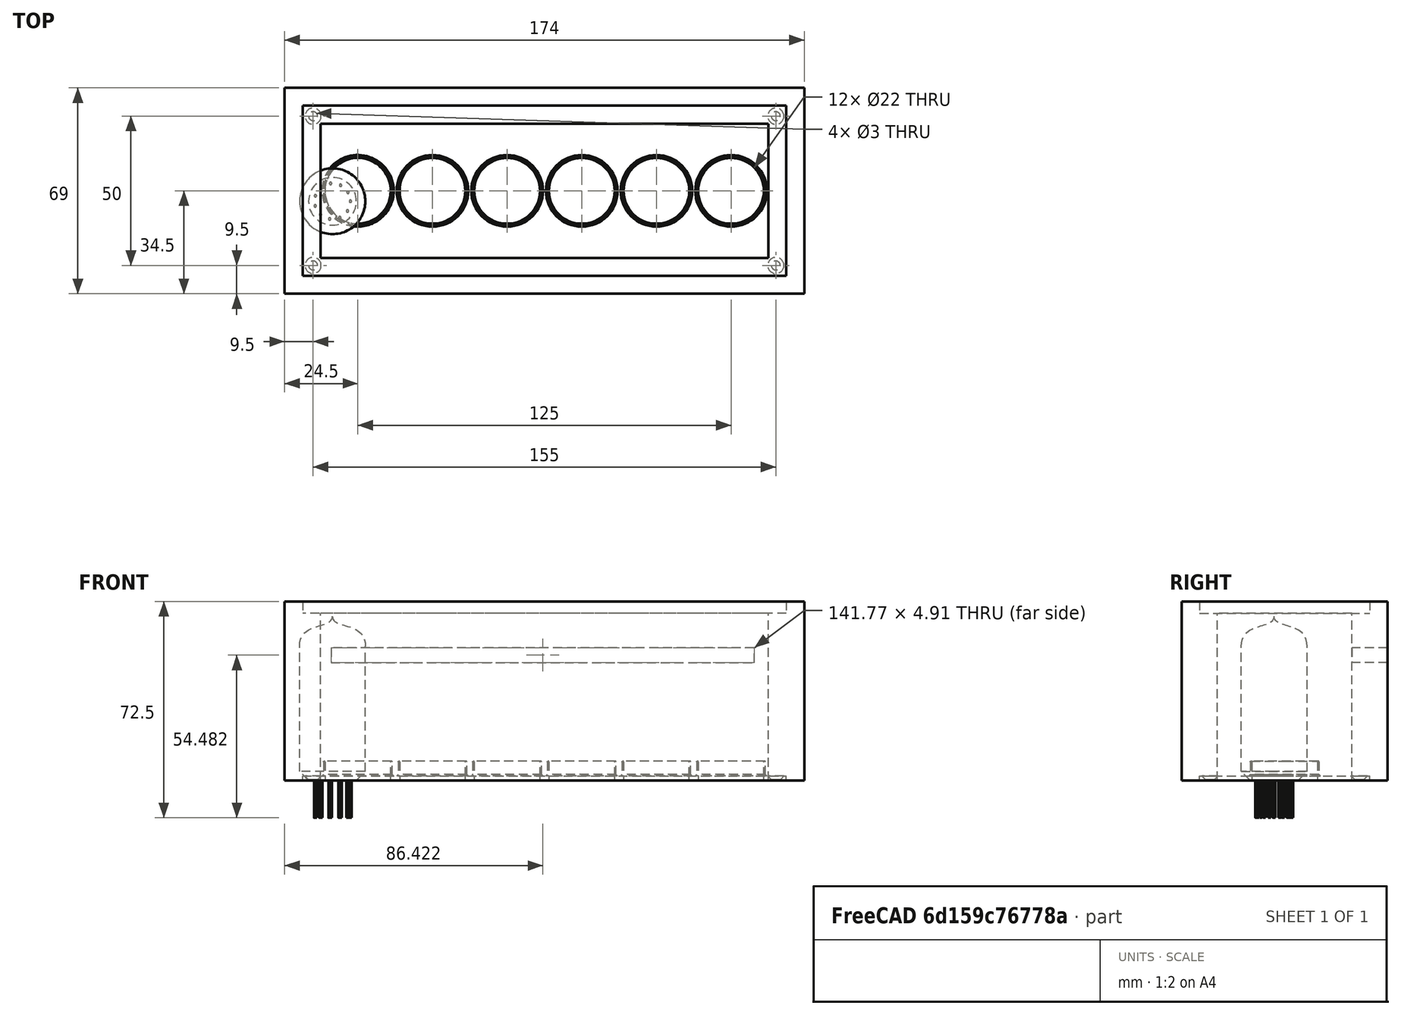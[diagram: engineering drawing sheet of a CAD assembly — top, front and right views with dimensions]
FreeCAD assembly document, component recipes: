
FREECAD ASSEMBLY — COMPONENT RECIPES ("aiometer")

This assembly document has 3 components, labeled P0..P2 below (a component is one placed body or linked part). 3 of them carry a construction recipe — the FreeCAD feature program that regenerates the part from scratch, quoted from this document or its linked companion documents; the rest are supplied as boundary geometry only. No exploded tour is included for this assembly.
COMPONENT P0 — recipe-attached ("Body", modeled in this document).
Construction recipe (the document's own serialized feature program — sketch geometry with constraints, then the solid features built on it; lengths are millimeters unless a unit is written):

FEATURE [Sketcher::SketchObject] Sketch  label="front"
  FullyConstrained = true
  MapMode = 5
  Support = -> [XY_Plane]
  sketch-geometry (4):
    g0: LineSegment StartX=162 StartY=-12 StartZ=0 EndX=150 EndY=0 EndZ=0
    g1: LineSegment StartX=150 StartY=0 StartZ=0 EndX=0 EndY=0 EndZ=0
    g2: LineSegment StartX=0 StartY=0 StartZ=0 EndX=-12 EndY=-12 EndZ=0
    g3: LineSegment StartX=-12 StartY=-12 StartZ=0 EndX=162 EndY=-12 EndZ=0
  constraints (11):
    c: Coincident(g0,g1)
    c: Horizontal(g1)
    c: DistanceX(g1,g1) = 150
    c: DistanceY(g0,g0) = 12
    c: Coincident(g-1,g1)
    c: Coincident(g1,g2)
    c: Coincident(g2,g3)
    c: Coincident(g3,g0)
    c: Horizontal(g3)
    c: Angle(g3,g2) = 0.785398
    c: Angle(g0,g3) = 0.785398
FEATURE [PartDesign::Pad] Pad  label="Front"
  Direction = (0,0,1)
  Length = 60
  Length2 = 10
  Profile = -> Sketch
  ReferenceAxis = -> Sketch [N_Axis]
  Type = 0
FEATURE [Sketcher::SketchObject] Sketch001  label="right"
  ExternalGeometry = -> [Pad,Sketch]
  FullyConstrained = true
  MapMode = 5
  Support = -> [XY_Plane]
  sketch-geometry (4):
    g0: LineSegment StartX=0 StartY=45 StartZ=0 EndX=0 EndY=0 EndZ=0
    g1: LineSegment StartX=0 StartY=0 StartZ=0 EndX=-12 EndY=-12 EndZ=0
    g2: LineSegment StartX=-12 StartY=-12 StartZ=0 EndX=-12 EndY=57 EndZ=0
    g3: LineSegment StartX=-12 StartY=57 StartZ=0 EndX=0 EndY=45 EndZ=0
  constraints (10):
    c: Vertical(g0)
    c: Coincident(g0,g-4)
    c: DistanceY(g0,g0) = 45
    c: Coincident(g0,g1)
    c: Coincident(g1,g2)
    c: Vertical(g2)
    c: Coincident(g2,g3)
    c: Coincident(g3,g0)
    c: Coincident(g1,g-5)
    c: Angle(g2,g3) = 0.785398
FEATURE [PartDesign::Pad] Pad001  label="Right"
  BaseFeature = -> Pad
  Direction = (0,0,1)
  Length = 60
  Length2 = 10
  Profile = -> Sketch001
  ReferenceAxis = -> Sketch001 [N_Axis]
  Type = 0
  expr: Length = Pad.Length
FEATURE [Sketcher::SketchObject] Sketch004  label="left"
  ExternalGeometry = -> [Sketch,Sketch001]
  FullyConstrained = true
  MapMode = 5
  Support = -> [XY_Plane]
  sketch-geometry (4):
    g0: LineSegment StartX=150 StartY=0 StartZ=0 EndX=162 EndY=-12 EndZ=0
    g1: LineSegment StartX=162 StartY=-12 StartZ=0 EndX=162 EndY=57 EndZ=0
    g2: LineSegment StartX=162 StartY=57 StartZ=0 EndX=150 EndY=45 EndZ=0
    g3: LineSegment StartX=150 StartY=45 StartZ=0 EndX=150 EndY=0 EndZ=0
  constraints (10):
    c: Coincident(g-4,g0)
    c: Coincident(g0,g-4)
    c: Coincident(g0,g1)
    c: Vertical(g1)
    c: Coincident(g1,g2)
    c: Coincident(g2,g3)
    c: Coincident(g3,g0)
    c: Vertical(g3)
    c: Equal(g3,g-5)
    c: Equal(g1,g-6)
FEATURE [PartDesign::Pad] Pad004  label="Left"
  BaseFeature = -> Pad001
  Direction = (0,0,1)
  Length = 60
  Length2 = 10
  Profile = -> Sketch004
  ReferenceAxis = -> Sketch004 [N_Axis]
  Type = 0
  expr: Length = Pad.Length
FEATURE [Sketcher::SketchObject] Sketch007  label="back"
  ExternalGeometry = -> [Pad004]
  FullyConstrained = true
  MapMode = 5
  Support = -> [XY_Plane]
  sketch-geometry (4):
    g0: LineSegment StartX=-12 StartY=57 StartZ=0 EndX=162 EndY=57 EndZ=0
    g1: LineSegment StartX=162 StartY=57 StartZ=0 EndX=150 EndY=45 EndZ=0
    g2: LineSegment StartX=150 StartY=45 StartZ=0 EndX=0 EndY=45 EndZ=0
    g3: LineSegment StartX=0 StartY=45 StartZ=0 EndX=-12 EndY=57 EndZ=0
  constraints (8):
    c: Coincident(g0,g-3)
    c: Coincident(g0,g-6)
    c: Coincident(g0,g1)
    c: Coincident(g1,g-5)
    c: Coincident(g1,g2)
    c: Coincident(g2,g-4)
    c: Coincident(g2,g3)
    c: Coincident(g3,g0)
FEATURE [PartDesign::Pad] Pad006  label="Back"
  BaseFeature = -> Pad004
  Direction = (0,0,1)
  Length = 60
  Length2 = 10
  Profile = -> Sketch007
  ReferenceAxis = -> Sketch007 [N_Axis]
  Type = 0
  expr: Length = Pad.Length
FEATURE [Sketcher::SketchObject] Sketch008  label="top_step"
  ExternalGeometry = -> [Pad006]
  FullyConstrained = true
  MapMode = 5
  Placement = pos=(0,0,60) rot=(0,0,1;0rad)
  Support = -> [Pad006]
  sketch-geometry (4):
    g0: LineSegment StartX=-6 StartY=51 StartZ=0 EndX=156 EndY=51 EndZ=0
    g1: LineSegment StartX=156 StartY=51 StartZ=0 EndX=156 EndY=-6 EndZ=0
    g2: LineSegment StartX=156 StartY=-6 StartZ=0 EndX=-6 EndY=-6 EndZ=0
    g3: LineSegment StartX=-6 StartY=-6 StartZ=0 EndX=-6 EndY=51 EndZ=0
  constraints (12):
    c: PointOnObject(g0,g-3)
    c: PointOnObject(g0,g-6)
    c: Horizontal(g0)
    c: Coincident(g0,g1)
    c: PointOnObject(g1,g-5)
    c: Vertical(g1)
    c: Coincident(g1,g2)
    c: PointOnObject(g2,g-4)
    c: Horizontal(g2)
    c: Coincident(g2,g3)
    c: Coincident(g3,g0)
    c: DistanceX(g2,g-4) = 6
FEATURE [PartDesign::Pocket] Pocket  label="Top_step"
  BaseFeature = -> Pad006
  Direction = (0,0,-1)
  Length = 4
  Length2 = 5
  Profile = -> Sketch008
  ReferenceAxis = -> Sketch008 [N_Axis]
  Type = 0
FEATURE [Sketcher::SketchObject] Sketch011
  FullyConstrained = false
  MapMode = 5
  Placement = pos=(0,57,0) rot=(0,0.707107,0.707107;3.14159rad)
  Support = -> [Pad006]
  sketch-geometry (4):
    g0: LineSegment StartX=-145.309 StartY=44.4355 StartZ=0 EndX=-3.53485 EndY=44.4355 EndZ=0
    g1: LineSegment StartX=-3.53485 StartY=44.4355 StartZ=0 EndX=-3.53485 EndY=39.5279 EndZ=0
    g2: LineSegment StartX=-3.53485 StartY=39.5279 StartZ=0 EndX=-145.309 EndY=39.5279 EndZ=0
    g3: LineSegment StartX=-145.309 StartY=39.5279 StartZ=0 EndX=-145.309 EndY=44.4355 EndZ=0
  constraints (8):
    c: Coincident(g0,g1)
    c: Coincident(g1,g2)
    c: Coincident(g2,g3)
    c: Coincident(g3,g0)
    c: Horizontal(g0)
    c: Horizontal(g2)
    c: Vertical(g1)
    c: Vertical(g3)
FEATURE [PartDesign::Pocket] Pocket001
  BaseFeature = -> Pocket
  Direction = (0,-1,2e-16)
  Length = 0
  Length2 = 5
  Profile = -> Sketch011
  ReferenceAxis = -> Sketch011 [N_Axis]
  Type = 2
FEATURE [PartDesign::CoordinateSystem] LCS_BODY  label="LCS_body"
  AttacherType = Attacher::AttachEngine3D
  MapMode = 5
  Placement = pos=(0,0,56) rot=(0,0,1;0rad)
  Support = -> [Pocket001]
FEATURE [PartDesign::Body] Body
  Group = -> [Sketch,Pad,Sketch001,Pad001,Pad004,Sketch004,Sketch007,Pad006,Sketch008,Pocket,Sketch011,Pocket001,LCS_BODY]
  Origin = -> Origin
  Tip = -> Pocket001
COMPONENT P1 — recipe-attached ("Top_sheet", modeled in this document).
Construction recipe (the document's own serialized feature program — sketch geometry with constraints, then the solid features built on it; lengths are millimeters unless a unit is written):

FEATURE [Sketcher::SketchObject] Sketch005  label="top"
  FullyConstrained = true
  MapMode = 5
  Support = -> [XY_Plane001]
  sketch-geometry (20):
    g0: LineSegment StartX=0 StartY=45 StartZ=0 EndX=150 EndY=45 EndZ=0
    g1: LineSegment StartX=150 StartY=45 StartZ=0 EndX=150 EndY=0 EndZ=0
    g2: LineSegment StartX=150 StartY=0 StartZ=0 EndX=0 EndY=0 EndZ=0
    g3: Circle CenterX=12.5 CenterY=22.5 CenterZ=0 NormalX=0 NormalY=0 NormalZ=1 AngleXU=0 Radius=11
    g4: Circle CenterX=37.5 CenterY=22.5 CenterZ=0 NormalX=0 NormalY=0 NormalZ=1 AngleXU=0 Radius=11
    g5: LineSegment StartX=12.5 StartY=22.5 StartZ=0 EndX=37.5 EndY=22.5 EndZ=0
    g6: Circle CenterX=62.5 CenterY=22.5 CenterZ=0 NormalX=0 NormalY=0 NormalZ=1 AngleXU=0 Radius=11
    g7: LineSegment StartX=37.5 StartY=22.5 StartZ=0 EndX=62.5 EndY=22.5 EndZ=0
    g8: Circle CenterX=87.5 CenterY=22.5 CenterZ=0 NormalX=0 NormalY=0 NormalZ=1 AngleXU=0 Radius=11
    g9: LineSegment StartX=62.5 StartY=22.5 StartZ=0 EndX=87.5 EndY=22.5 EndZ=0
    g10: Circle CenterX=112.5 CenterY=22.5 CenterZ=0 NormalX=0 NormalY=0 NormalZ=1 AngleXU=0 Radius=11
    g11: LineSegment StartX=87.5 StartY=22.5 StartZ=0 EndX=112.5 EndY=22.5 EndZ=0
    g12: Circle CenterX=137.5 CenterY=22.5 CenterZ=0 NormalX=0 NormalY=0 NormalZ=1 AngleXU=0 Radius=11
    g13: LineSegment StartX=112.5 StartY=22.5 StartZ=0 EndX=137.5 EndY=22.5 EndZ=0
    g14: LineSegment StartX=0 StartY=45 StartZ=0 EndX=0 EndY=0 EndZ=0
    g15: LineSegment StartX=-6 StartY=51 StartZ=0 EndX=156 EndY=51 EndZ=0
    g16: LineSegment StartX=156 StartY=51 StartZ=0 EndX=156 EndY=-6 EndZ=0
    g17: LineSegment StartX=156 StartY=-6 StartZ=0 EndX=-6 EndY=-6 EndZ=0
    g18: LineSegment StartX=-6 StartY=-6 StartZ=0 EndX=-6 EndY=51 EndZ=0
    g19: LineSegment StartX=75 StartY=45 StartZ=0 EndX=75 EndY=0 EndZ=0
  constraints (51):
    c: Coincident(g0,g1)
    c: Coincident(g1,g2)
    c: Horizontal(g0)
    c: Horizontal(g2)
    c: Vertical(g1)
    c: Diameter(g3) = 22
    c: Coincident(g3,g5)
    c: Coincident(g4,g5)
    c: Distance(g5) = 25
    c: Angle(g5) = 0
    c: Coincident(g4,g7)
    c: Coincident(g6,g7)
    c: Equal(g5,g7)
    c: Parallel(g7,g5)
    c: Coincident(g6,g9)
    c: Coincident(g8,g9)
    c: Equal(g5,g9)
    c: Parallel(g9,g5)
    c: Coincident(g8,g11)
    c: Coincident(g10,g11)
    c: Equal(g5,g11)
    c: Parallel(g11,g5)
    c: Coincident(g10,g13)
    c: Coincident(g12,g13)
    c: Equal(g5,g13)
    c: Parallel(g13,g5)
    c: DistanceX(g2,g2) = 150
    c: Coincident(g14,g0)
    c: Coincident(g14,g2)
    c: Coincident(g-1,g2)
    c: Coincident(g15,g16)
    c: Coincident(g16,g17)
    c: Coincident(g17,g18)
    c: Coincident(g18,g15)
    c: Horizontal(g15)
    c: Vertical(g18)
    c: DistanceY(g14,g14) = 45
    c: Equal(g4,g3)
    c: Equal(g3,g6)
    c: Equal(g3,g8)
    c: Equal(g3,g10)
    c: Equal(g3,g12)
    c: Symmetric(g0,g2,g5)
    c: DistanceX(g2,g3) = 12.5
    c: Symmetric(g15,g16,g13)
    c: PointOnObject(g19,g0)
    c: PointOnObject(g19,g2)
    c: Symmetric(g17,g16,g19)
    c: DistanceX(g17,g2) = 6
    c: DistanceY(g17,g2) = 6
    c: Symmetric(g2,g1,g19)
FEATURE [PartDesign::Pad] Pad005  label="Top"
  Direction = (0,0,1)
  Length = 1.5
  Length2 = 10
  Profile = -> Sketch005
  ReferenceAxis = -> Sketch005 [N_Axis]
  Type = 0
FEATURE [Sketcher::SketchObject] Sketch009
  ExternalGeometry = -> [Pad005]
  FullyConstrained = true
  MapMode = 5
  Placement = pos=(0,0,1.5) rot=(0,0,1;0rad)
  Support = -> [Pad005]
  sketch-geometry (10):
    g0: Circle CenterX=152.5 CenterY=47.5 CenterZ=0 NormalX=0 NormalY=0 NormalZ=1 AngleXU=0 Radius=1.5
    g1: Circle CenterX=-2.5 CenterY=47.5 CenterZ=0 NormalX=0 NormalY=0 NormalZ=1 AngleXU=0 Radius=1.5
    g2: LineSegment StartX=-2.5 StartY=47.5 StartZ=0 EndX=152.5 EndY=47.5 EndZ=0
    g3: LineSegment StartX=-2.5 StartY=47.5 StartZ=0 EndX=-2.5 EndY=-2.5 EndZ=0
    g4: LineSegment StartX=152.5 StartY=47.5 StartZ=0 EndX=152.5 EndY=-2.5 EndZ=0
    g5: LineSegment StartX=-2.5 StartY=-2.5 StartZ=0 EndX=152.5 EndY=-2.5 EndZ=0
    g6: LineSegment StartX=75 StartY=47.5 StartZ=0 EndX=75 EndY=-2.5 EndZ=0
    g7: LineSegment StartX=-2.5 StartY=22.5 StartZ=0 EndX=152.5 EndY=22.5 EndZ=0
    g8: Circle CenterX=-2.5 CenterY=-2.5 CenterZ=0 NormalX=0 NormalY=0 NormalZ=1 AngleXU=0 Radius=1.5
    g9: Circle CenterX=152.5 CenterY=-2.5 CenterZ=0 NormalX=0 NormalY=0 NormalZ=1 AngleXU=0 Radius=1.5
  constraints (24):
    c: Horizontal(g2)
    c: Vertical(g4)
    c: Coincident(g3,g2)
    c: Coincident(g2,g4)
    c: Coincident(g5,g3)
    c: Coincident(g5,g4)
    c: DistanceX(g-4,g2) = 3.5
    c: DistanceY(g2,g-4) = 3.5
    c: PointOnObject(g6,g2)
    c: PointOnObject(g6,g5)
    c: PointOnObject(g7,g3)
    c: PointOnObject(g7,g4)
    c: Symmetric(g-5,g-6,g6)
    c: Symmetric(g-4,g-5,g7)
    c: Symmetric(g3,g4,g6)
    c: Symmetric(g3,g2,g7)
    c: Diameter(g1) = 3
    c: Coincident(g1,g2)
    c: Equal(g0,g1)
    c: Coincident(g0,g2)
    c: Equal(g1,g8)
    c: Equal(g1,g9)
    c: Coincident(g3,g8)
    c: Coincident(g9,g4)
FEATURE [PartDesign::Hole] Hole
  BaseFeature = -> Pad005
  CustomThreadClearance = 0
  Depth = 25
  DepthType = 0
  Diameter = 3
  DrillForDepth = false
  DrillPoint = 0
  DrillPointAngle = 118
  HoleCutCountersinkAngle = 90
  HoleCutCustomValues = false
  HoleCutDepth = 0
  HoleCutDiameter = 5.4
  HoleCutType = 2
  ModelThread = false
  Profile = -> Sketch009
  Tapered = false
  TaperedAngle = 90
  ThreadClass = 0
  ThreadDepth = 25
  ThreadDepthType = 0
  ThreadDirection = 0
  ThreadFit = 0
  ThreadSize = 0
  ThreadType = 0
  Threaded = false
  UseCustomThreadClearance = false
FEATURE [Sketcher::SketchObject] Sketch010  label="tube_stub"
  ExternalGeometry = -> [Hole]
  FullyConstrained = true
  MapMode = 5
  Placement = pos=(0,0,1.5) rot=(0,0,1;0rad)
  Support = -> [Hole]
  sketch-geometry (12):
    g0: Circle CenterX=12.5 CenterY=22.5 CenterZ=0 NormalX=0 NormalY=0 NormalZ=1 AngleXU=0 Radius=11
    g1: Circle CenterX=12.5 CenterY=22.5 CenterZ=0 NormalX=0 NormalY=0 NormalZ=1 AngleXU=0 Radius=11.5
    g2: Circle CenterX=37.5 CenterY=22.5 CenterZ=0 NormalX=0 NormalY=0 NormalZ=1 AngleXU=0 Radius=11
    g3: Circle CenterX=37.5 CenterY=22.5 CenterZ=0 NormalX=0 NormalY=0 NormalZ=1 AngleXU=0 Radius=11.5
    g4: Circle CenterX=62.5 CenterY=22.5 CenterZ=0 NormalX=0 NormalY=0 NormalZ=1 AngleXU=0 Radius=11
    g5: Circle CenterX=62.5 CenterY=22.5 CenterZ=0 NormalX=0 NormalY=0 NormalZ=1 AngleXU=0 Radius=11.5
    g6: Circle CenterX=87.5 CenterY=22.5 CenterZ=0 NormalX=0 NormalY=0 NormalZ=1 AngleXU=0 Radius=11
    g7: Circle CenterX=87.5 CenterY=22.5 CenterZ=0 NormalX=0 NormalY=0 NormalZ=1 AngleXU=0 Radius=11.5
    g8: Circle CenterX=112.5 CenterY=22.5 CenterZ=0 NormalX=0 NormalY=0 NormalZ=1 AngleXU=0 Radius=11
    g9: Circle CenterX=137.5 CenterY=22.5 CenterZ=0 NormalX=0 NormalY=0 NormalZ=1 AngleXU=0 Radius=11
    g10: Circle CenterX=112.5 CenterY=22.5 CenterZ=0 NormalX=0 NormalY=0 NormalZ=1 AngleXU=0 Radius=11.5
    g11: Circle CenterX=137.5 CenterY=22.5 CenterZ=0 NormalX=0 NormalY=0 NormalZ=1 AngleXU=0 Radius=11.5
  constraints (24):
    c: Coincident(g0,g-3)
    c: Equal(g0,g-3)
    c: Coincident(g1,g0)
    c: Coincident(g2,g-4)
    c: Equal(g-4,g2)
    c: Coincident(g3,g2)
    c: Coincident(g4,g-5)
    c: Equal(g4,g-5)
    c: Coincident(g5,g4)
    c: Coincident(g6,g-6)
    c: Equal(g6,g-6)
    c: Coincident(g7,g6)
    c: Coincident(g8,g-7)
    c: Coincident(g9,g-8)
    c: Coincident(g10,g8)
    c: Coincident(g11,g9)
    c: Equal(g-7,g8)
    c: Equal(g9,g-8)
    c: Diameter(g1) = 23
    c: Equal(g1,g3)
    c: Equal(g5,g7)
    c: Equal(g10,g11)
    c: Equal(g11,g1)
    c: Equal(g7,g1)
FEATURE [PartDesign::Pad] Pad007  label="Tube_stub"
  BaseFeature = -> Hole
  Direction = (0,0,1)
  Length = 5
  Length2 = 10
  Profile = -> Sketch010
  ReferenceAxis = -> Sketch010 [N_Axis]
  Type = 0
FEATURE [PartDesign::Fillet] Fillet
  Base = -> Pad007 [Face34,Face35,Face36,Face37,Face38,Face33]
  BaseFeature = -> Pad007
  Radius = 0.24
  SupportTransform = false
  UseAllEdges = false
FEATURE [PartDesign::Chamfer] Chamfer
  Angle = 45
  Base = -> Fillet [Face1,Face11,Face12,Face14,Face15,Face16]
  BaseFeature = -> Fillet
  ChamferType = 0
  FlipDirection = false
  Size = 0.5
  Size2 = 1
  SupportTransform = false
  UseAllEdges = false
FEATURE [PartDesign::CoordinateSystem] LCS_t1
  AttacherType = Attacher::AttachEngine3D
  MapMode = 11
  Placement = pos=(12.5,22.5,0) rot=(0,0,1;1.5708rad)
  Support = -> [Chamfer]
FEATURE [PartDesign::CoordinateSystem] LCS_t2
  AttacherType = Attacher::AttachEngine3D
  MapMode = 11
  Placement = pos=(37.5,22.5,0) rot=(0,0,1;1.5708rad)
  Support = -> [Chamfer]
FEATURE [PartDesign::CoordinateSystem] LCS_t3001  label="LCS_t3"
  AttacherType = Attacher::AttachEngine3D
  MapMode = 11
  Placement = pos=(62.5,22.5,0) rot=(0,0,1;1.5708rad)
  Support = -> [Chamfer]
FEATURE [PartDesign::CoordinateSystem] LCS_t4
  AttacherType = Attacher::AttachEngine3D
  MapMode = 11
  Placement = pos=(87.5,22.5,0) rot=(0,0,1;1.5708rad)
  Support = -> [Chamfer]
FEATURE [PartDesign::CoordinateSystem] LCS_t5
  AttacherType = Attacher::AttachEngine3D
  MapMode = 11
  Placement = pos=(112.5,22.5,0) rot=(0,0,1;1.5708rad)
  Support = -> [Chamfer]
FEATURE [PartDesign::CoordinateSystem] LCS_t6
  AttacherType = Attacher::AttachEngine3D
  MapMode = 11
  Placement = pos=(137.5,22.5,0) rot=(0,0,1;1.5708rad)
  Support = -> [Chamfer]
FEATURE [PartDesign::CoordinateSystem] LCS_sheet
  AttacherType = Attacher::AttachEngine3D
  MapMode = 2
  Support = -> [Chamfer]
FEATURE [PartDesign::Body] Body001  label="Top_sheet"
  Group = -> [Sketch005,Pad005,Sketch009,Hole,Sketch010,Pad007,Fillet,Chamfer,LCS_t1,LCS_t2,LCS_t3001,LCS_t4,LCS_t5,LCS_t6,LCS_sheet]
  Origin = -> Origin001
  Tip = -> Chamfer
COMPONENT P2 — recipe-attached ("VFDtube", modeled in this document).
Construction recipe (the document's own serialized feature program — sketch geometry with constraints, then the solid features built on it; lengths are millimeters unless a unit is written):

FEATURE [Sketcher::SketchObject] Sketch012  label="tube"
  FullyConstrained = false
  MapMode = 5
  Placement = pos=(0,0,0) rot=(1,0,0;1.5708rad)
  Support = -> [XZ_Plane003]
  sketch-geometry (10):
    g0: LineSegment StartX=0 StartY=55 StartZ=0 EndX=0 EndY=0 EndZ=0
    g1: LineSegment StartX=0 StartY=0 StartZ=0 EndX=11 EndY=0 EndZ=0
    g2: LineSegment StartX=11 StartY=0 StartZ=0 EndX=11 EndY=45 EndZ=0
    g3-g6: Circle x4 (B-spline internal-alignment scaffolding for g7; pole/knot coordinates omitted)
    g7: BSplineCurve PolesCount=4 KnotsCount=2 Degree=3 IsPeriodic=0
    g8: GeomPoint X=0 Y=55 Z=0
    g9: GeomPoint X=11 Y=45 Z=0
  constraints (20):
    c: PointOnObject(g0,g-2)
    c: Coincident(g0,g-1)
    c: Coincident(g0,g1)
    c: Horizontal(g1)
    c: Coincident(g1,g2)
    c: Vertical(g2)
    c: DistanceX(g1,g1) = 11
    c: DistanceY(g0,g0) = 55
    c: DistanceY(g2,g2) = 45
    c: Weight(g3) = 1
    c: Coincident(g7,g0)
    c: Equal(g3,g4)
    c: Equal(g3,g5)
    c: Equal(g3,g6)
    c: Coincident(g7,g2)
    c: InternalAlignment(g3-g6 -> g7) x4
    c: InternalAlignment(g8,g7)
    c: InternalAlignment(g9,g7)
    c: Vertical(g2,g5)
    c: PointOnObject(g4,g0)
FEATURE [PartDesign::Revolution] Revolution  label="Tube"
  Angle = 360
  Axis = (0,-2e-16,1)
  Base = (0,0,0)
  Placement = pos=(0,0,0) rot=(1,0,0;1.5708rad)
  Profile = -> Sketch012
  ReferenceAxis = -> Sketch012 [V_Axis]
  Reversed = true
FEATURE [Sketcher::SketchObject] Sketch013
  FullyConstrained = true
  MapMode = 5
  Placement = pos=(0,0,0) rot=(1,0,0;3.14159rad)
  Support = -> [Revolution]
  sketch-geometry (1):
    g0: Circle CenterX=6 CenterY=0 CenterZ=0 NormalX=0 NormalY=0 NormalZ=1 AngleXU=0 Radius=0.4
  constraints (3):
    c: Diameter(g0) = 0.8
    c: DistanceX(g-1,g0) = 6
    c: PointOnObject(g0,g-1)
FEATURE [PartDesign::Chamfer] Chamfer001
  Angle = 45
  Base = -> Revolution [Edge1]
  BaseFeature = -> Revolution
  ChamferType = 0
  FlipDirection = false
  Placement = pos=(0,0,0) rot=(1,0,0;1.5708rad)
  Size = 3
  Size2 = 1
  SupportTransform = false
  UseAllEdges = false
FEATURE [PartDesign::Pad] Pad008  label="Lead"
  BaseFeature = -> Chamfer001
  Direction = (0,2e-16,-1)
  Length = 12.5
  Length2 = 10
  Placement = pos=(0,0,0) rot=(1,0,0;1.5708rad)
  Profile = -> Sketch013
  ReferenceAxis = -> Sketch013 [N_Axis]
  Type = 0
FEATURE [PartDesign::PolarPattern] PolarPattern  label="Leads"
  Angle = 330
  Axis = -> Sketch013 [N_Axis]
  BaseFeature = -> Pad008
  Occurrences = 11
  Originals = -> [Pad008]
  Placement = pos=(0,0,0) rot=(1,0,0;1.5708rad)
FEATURE [PartDesign::CoordinateSystem] LCS_tube
  AttacherType = Attacher::AttachEngine3D
  MapMode = 11
  Placement = pos=(0,7e-16,3) rot=(0,0,1;1.5708rad)
  Support = -> [PolarPattern]
FEATURE [PartDesign::Body] Body002  label="VFDtube"
  Group = -> [Sketch012,Revolution,Chamfer001,Sketch013,Pad008,PolarPattern,LCS_tube]
  Origin = -> Origin003
  Placement = pos=(4,19,0) rot=(0,0,1;0rad)
  Tip = -> PolarPattern
PROVENANCE & LICENSES
A FreeCAD (.FCStd) document from a public repository crawl; recipes are the document's own serialized feature recipes (and, for linked parts, companion documents' recipes).
License: gpl-3.0.
